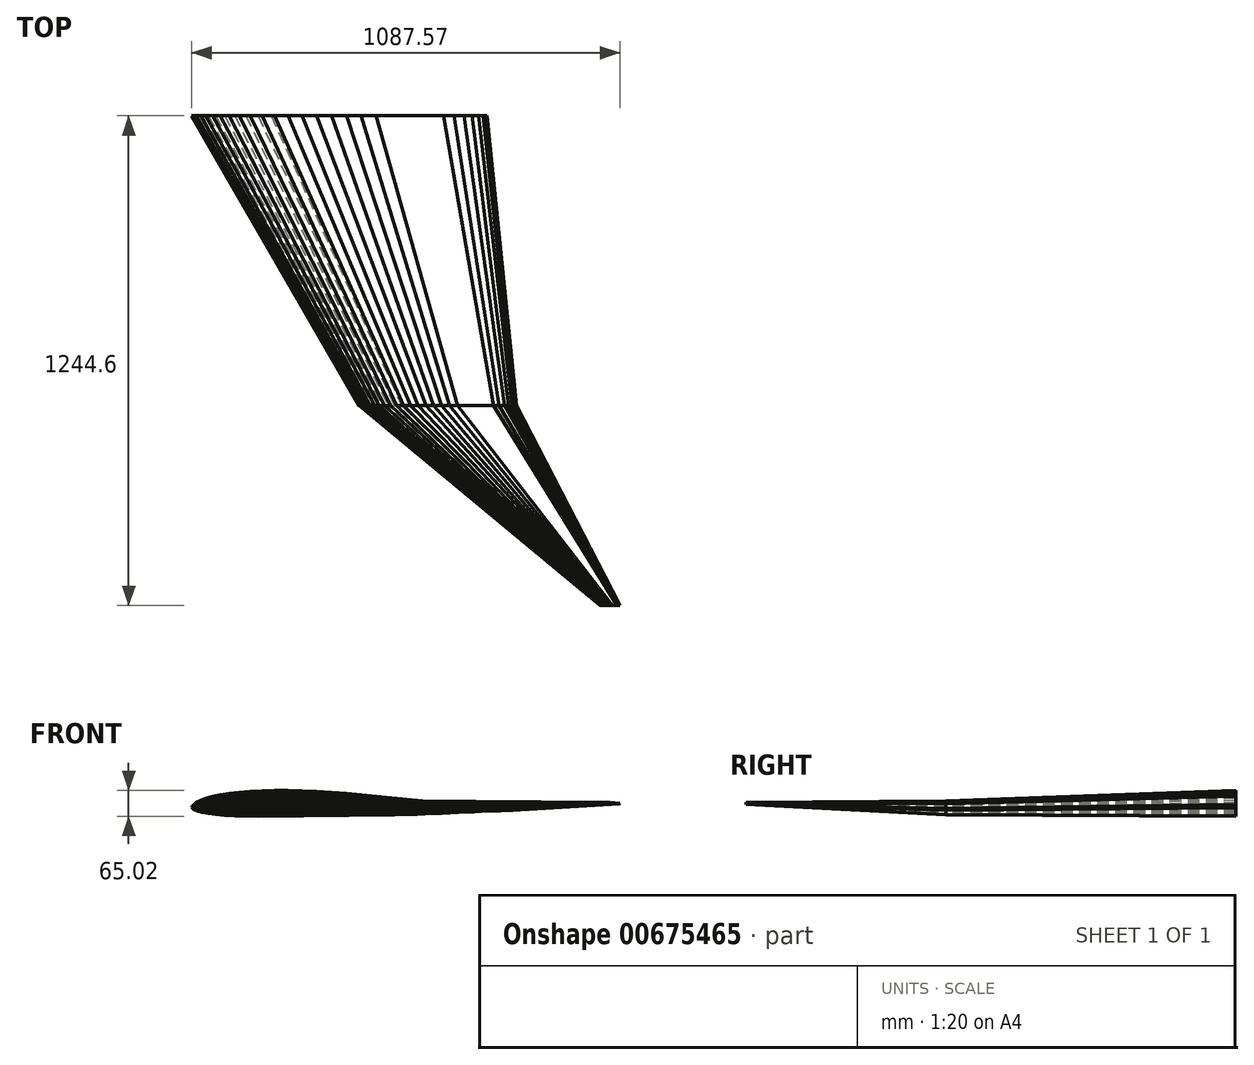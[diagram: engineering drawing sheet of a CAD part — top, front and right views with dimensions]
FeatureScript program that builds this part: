
annotation { "Feature Type Name" : "Feature", "Feature Type Description" : "" }
export const myFeature = defineFeature(function(context is Context, id is Id, definition is map)
    precondition{}
    {
        {
            var Q0;
            Q0=qCreatedBy(makeId("Front.planeOp"),FACE);
            var sketch = newSketch(context, id + "F0", { "sketchPlane" : qUnion([Q0])});
            skLineSegment(sketch, "E0", {"start": v(375, -10.05) * mm, "end": v(372.59, -10.06) * mm});
            skLineSegment(sketch, "E1", {"start": v(372.59, -10.06) * mm, "end": v(365.32, -10) * mm});
            skLineSegment(sketch, "E2", {"start": v(365.32, -10) * mm, "end": v(353.32, -9.6) * mm});
            skLineSegment(sketch, "E3", {"start": v(353.32, -9.6) * mm, "end": v(336.87, -8.71) * mm});
            skLineSegment(sketch, "E4", {"start": v(336.87, -8.71) * mm, "end": v(316.26, -7.24) * mm});
            skLineSegment(sketch, "E5", {"start": v(316.26, -7.24) * mm, "end": v(291.86, -5.09) * mm});
            skLineSegment(sketch, "E6", {"start": v(291.86, -5.09) * mm, "end": v(264.18, -2.25) * mm});
            skLineSegment(sketch, "E7", {"start": v(264.18, -2.25) * mm, "end": v(233.7, 1.18) * mm});
            skLineSegment(sketch, "E8", {"start": v(233.7, 1.18) * mm, "end": v(200.89, 5.09) * mm});
            skLineSegment(sketch, "E9", {"start": v(200.89, 5.09) * mm, "end": v(166.24, 9.3) * mm});
            skLineSegment(sketch, "E10", {"start": v(166.24, 9.3) * mm, "end": v(130.24, 13.62) * mm});
            skLineSegment(sketch, "E11", {"start": v(130.24, 13.62) * mm, "end": v(93.27, 17.8) * mm});
            skLineSegment(sketch, "E12", {"start": v(93.27, 17.8) * mm, "end": v(55.7, 21.63) * mm});
            skLineSegment(sketch, "E13", {"start": v(55.7, 21.63) * mm, "end": v(17.83, 25) * mm});
            skLineSegment(sketch, "E14", {"start": v(17.83, 25) * mm, "end": v(-20.02, 27.78) * mm});
            skLineSegment(sketch, "E15", {"start": v(-20.02, 27.78) * mm, "end": v(-57.5, 29.97) * mm});
            skLineSegment(sketch, "E16", {"start": v(-57.5, 29.97) * mm, "end": v(-94.23, 31.51) * mm});
            skLineSegment(sketch, "E17", {"start": v(-94.23, 31.51) * mm, "end": v(-129.86, 32.37) * mm});
            skLineSegment(sketch, "E18", {"start": v(-129.86, 32.37) * mm, "end": v(-164.03, 32.5) * mm});
            skLineSegment(sketch, "E19", {"start": v(-164.03, 32.5) * mm, "end": v(-196.4, 31.89) * mm});
            skLineSegment(sketch, "E20", {"start": v(-196.4, 31.89) * mm, "end": v(-226.7, 30.47) * mm});
            skLineSegment(sketch, "E21", {"start": v(-226.7, 30.47) * mm, "end": v(-254.68, 28.27) * mm});
            skLineSegment(sketch, "E22", {"start": v(-254.68, 28.27) * mm, "end": v(-280.12, 25.33) * mm});
            skLineSegment(sketch, "E23", {"start": v(-280.12, 25.33) * mm, "end": v(-302.8, 21.7) * mm});
            skLineSegment(sketch, "E24", {"start": v(-302.8, 21.7) * mm, "end": v(-322.57, 17.45) * mm});
            skLineSegment(sketch, "E25", {"start": v(-322.57, 17.45) * mm, "end": v(-339.3, 12.66) * mm});
            skLineSegment(sketch, "E26", {"start": v(-339.3, 12.66) * mm, "end": v(-352.9, 7.47) * mm});
            skLineSegment(sketch, "E27", {"start": v(-352.9, 7.47) * mm, "end": v(-363.34, 2.06) * mm});
            skLineSegment(sketch, "E28", {"start": v(-363.34, 2.06) * mm, "end": v(-370.58, -3.28) * mm});
            skLineSegment(sketch, "E29", {"start": v(-370.58, -3.28) * mm, "end": v(-374.56, -8.12) * mm});
            skLineSegment(sketch, "E30", {"start": v(-374.56, -8.12) * mm, "end": v(-375, -10.05) * mm});
            skLineSegment(sketch, "E31", {"start": v(-375, -10.05) * mm, "end": v(-374.42, -12) * mm});
            skLineSegment(sketch, "E32", {"start": v(-374.42, -12) * mm, "end": v(-369.82, -15.48) * mm});
            skLineSegment(sketch, "E33", {"start": v(-369.82, -15.48) * mm, "end": v(-361.28, -19.05) * mm});
            skLineSegment(sketch, "E34", {"start": v(-361.28, -19.05) * mm, "end": v(-349.03, -22.44) * mm});
            skLineSegment(sketch, "E35", {"start": v(-349.03, -22.44) * mm, "end": v(-333.25, -25.53) * mm});
            skLineSegment(sketch, "E36", {"start": v(-333.25, -25.53) * mm, "end": v(-314.1, -28.15) * mm});
            skLineSegment(sketch, "E37", {"start": v(-314.1, -28.15) * mm, "end": v(-291.71, -30.2) * mm});
            skLineSegment(sketch, "E38", {"start": v(-291.71, -30.2) * mm, "end": v(-266.22, -31.6) * mm});
            skLineSegment(sketch, "E39", {"start": v(-266.22, -31.6) * mm, "end": v(-237.8, -32.35) * mm});
            skLineSegment(sketch, "E40", {"start": v(-237.8, -32.35) * mm, "end": v(-206.66, -32.5) * mm});
            skLineSegment(sketch, "E41", {"start": v(-206.66, -32.5) * mm, "end": v(-173.08, -32.14) * mm});
            skLineSegment(sketch, "E42", {"start": v(-173.08, -32.14) * mm, "end": v(-137.42, -31.32) * mm});
            skLineSegment(sketch, "E43", {"start": v(-137.42, -31.32) * mm, "end": v(-100.01, -30.12) * mm});
            skLineSegment(sketch, "E44", {"start": v(-100.01, -30.12) * mm, "end": v(-61.28, -28.63) * mm});
            skLineSegment(sketch, "E45", {"start": v(-61.28, -28.63) * mm, "end": v(-21.66, -26.96) * mm});
            skLineSegment(sketch, "E46", {"start": v(-21.66, -26.96) * mm, "end": v(18.39, -25.17) * mm});
            skLineSegment(sketch, "E47", {"start": v(18.39, -25.17) * mm, "end": v(58.39, -23.36) * mm});
            skLineSegment(sketch, "E48", {"start": v(58.39, -23.36) * mm, "end": v(97.83, -21.59) * mm});
            skLineSegment(sketch, "E49", {"start": v(97.83, -21.59) * mm, "end": v(136.25, -19.88) * mm});
            skLineSegment(sketch, "E50", {"start": v(136.25, -19.88) * mm, "end": v(173.15, -18.28) * mm});
            skLineSegment(sketch, "E51", {"start": v(173.15, -18.28) * mm, "end": v(208.1, -16.81) * mm});
            skLineSegment(sketch, "E52", {"start": v(208.1, -16.81) * mm, "end": v(240.67, -15.48) * mm});
            skLineSegment(sketch, "E53", {"start": v(240.67, -15.48) * mm, "end": v(270.44, -14.32) * mm});
            skLineSegment(sketch, "E54", {"start": v(270.44, -14.32) * mm, "end": v(297.05, -13.32) * mm});
            skLineSegment(sketch, "E55", {"start": v(297.05, -13.32) * mm, "end": v(320.16, -12.48) * mm});
            skLineSegment(sketch, "E56", {"start": v(320.16, -12.48) * mm, "end": v(339.47, -11.77) * mm});
            skLineSegment(sketch, "E57", {"start": v(339.47, -11.77) * mm, "end": v(354.75, -11.17) * mm});
            skLineSegment(sketch, "E58", {"start": v(354.75, -11.17) * mm, "end": v(365.83, -10.62) * mm});
            skLineSegment(sketch, "E59", {"start": v(365.83, -10.62) * mm, "end": v(372.65, -10.2) * mm});
            skLineSegment(sketch, "E60", {"start": v(372.65, -10.2) * mm, "end": v(375, -10.05) * mm});
            skLineSegment(sketch, "E61", {"start": v(-375, -10.05) * mm, "end": v(375, -10.05) * mm});
            skSolve(sketch);
        }
        {
            var Q0;
            Q0=qCreatedBy(makeId("Front.planeOp"),FACE);
            cPlane(context, id + "F1", {"entities" : qUnion([Q0]), "cplaneType" : CPlaneType.OFFSET, "offset" : 736.6 * mm, "width" : 152.4 * mm, "height" : 152.4 * mm});
        }
        {
            var Q0;
            Q0=qCreatedBy(id+"F1.planeOp",FACE);
            var sketch = newSketch(context, id + "F2", { "sketchPlane" : qUnion([Q0])});
            skLineSegment(sketch, "E62", {"start": v(450.55, -16.79) * mm, "end": v(449.26, -16.8) * mm});
            skLineSegment(sketch, "E63", {"start": v(449.26, -16.8) * mm, "end": v(445.39, -16.76) * mm});
            skLineSegment(sketch, "E64", {"start": v(445.39, -16.76) * mm, "end": v(438.99, -16.55) * mm});
            skLineSegment(sketch, "E65", {"start": v(438.99, -16.55) * mm, "end": v(430.21, -16.08) * mm});
            skLineSegment(sketch, "E66", {"start": v(430.21, -16.08) * mm, "end": v(419.22, -15.3) * mm});
            skLineSegment(sketch, "E67", {"start": v(419.22, -15.3) * mm, "end": v(406.2, -14.14) * mm});
            skLineSegment(sketch, "E68", {"start": v(406.2, -14.14) * mm, "end": v(391.45, -12.63) * mm});
            skLineSegment(sketch, "E69", {"start": v(391.45, -12.63) * mm, "end": v(375.19, -10.8) * mm});
            skLineSegment(sketch, "E70", {"start": v(375.19, -10.8) * mm, "end": v(357.69, -8.72) * mm});
            skLineSegment(sketch, "E71", {"start": v(357.69, -8.72) * mm, "end": v(339.21, -6.47) * mm});
            skLineSegment(sketch, "E72", {"start": v(339.21, -6.47) * mm, "end": v(320, -4.17) * mm});
            skLineSegment(sketch, "E73", {"start": v(320, -4.17) * mm, "end": v(300.3, -1.94) * mm});
            skLineSegment(sketch, "E74", {"start": v(300.3, -1.94) * mm, "end": v(280.25, 0.1) * mm});
            skLineSegment(sketch, "E75", {"start": v(280.25, 0.1) * mm, "end": v(260.06, 1.9) * mm});
            skLineSegment(sketch, "E76", {"start": v(260.06, 1.9) * mm, "end": v(239.87, 3.39) * mm});
            skLineSegment(sketch, "E77", {"start": v(239.87, 3.39) * mm, "end": v(219.89, 4.55) * mm});
            skLineSegment(sketch, "E78", {"start": v(219.89, 4.55) * mm, "end": v(200.3, 5.38) * mm});
            skLineSegment(sketch, "E79", {"start": v(200.3, 5.38) * mm, "end": v(181.29, 5.83) * mm});
            skLineSegment(sketch, "E80", {"start": v(181.29, 5.83) * mm, "end": v(163.07, 5.9) * mm});
            skLineSegment(sketch, "E81", {"start": v(163.07, 5.9) * mm, "end": v(145.8, 5.58) * mm});
            skLineSegment(sketch, "E82", {"start": v(145.8, 5.58) * mm, "end": v(129.64, 4.82) * mm});
            skLineSegment(sketch, "E83", {"start": v(129.64, 4.82) * mm, "end": v(114.72, 3.65) * mm});
            skLineSegment(sketch, "E84", {"start": v(114.72, 3.65) * mm, "end": v(101.15, 2.08) * mm});
            skLineSegment(sketch, "E85", {"start": v(101.15, 2.08) * mm, "end": v(89.05, 0.14) * mm});
            skLineSegment(sketch, "E86", {"start": v(89.05, 0.14) * mm, "end": v(78.5, -2.12) * mm});
            skLineSegment(sketch, "E87", {"start": v(78.5, -2.12) * mm, "end": v(69.6, -4.68) * mm});
            skLineSegment(sketch, "E88", {"start": v(69.6, -4.68) * mm, "end": v(62.34, -7.45) * mm});
            skLineSegment(sketch, "E89", {"start": v(62.34, -7.45) * mm, "end": v(56.77, -10.33) * mm});
            skLineSegment(sketch, "E90", {"start": v(56.77, -10.33) * mm, "end": v(52.9, -13.18) * mm});
            skLineSegment(sketch, "E91", {"start": v(52.9, -13.18) * mm, "end": v(50.79, -15.76) * mm});
            skLineSegment(sketch, "E92", {"start": v(50.79, -15.76) * mm, "end": v(50.55, -16.79) * mm});
            skLineSegment(sketch, "E93", {"start": v(50.55, -16.79) * mm, "end": v(50.86, -17.83) * mm});
            skLineSegment(sketch, "E94", {"start": v(50.86, -17.83) * mm, "end": v(53.3, -19.68) * mm});
            skLineSegment(sketch, "E95", {"start": v(53.3, -19.68) * mm, "end": v(57.87, -21.59) * mm});
            skLineSegment(sketch, "E96", {"start": v(57.87, -21.59) * mm, "end": v(64.4, -23.4) * mm});
            skLineSegment(sketch, "E97", {"start": v(64.4, -23.4) * mm, "end": v(72.81, -25.04) * mm});
            skLineSegment(sketch, "E98", {"start": v(72.81, -25.04) * mm, "end": v(83.03, -26.44) * mm});
            skLineSegment(sketch, "E99", {"start": v(83.03, -26.44) * mm, "end": v(94.97, -27.53) * mm});
            skLineSegment(sketch, "E100", {"start": v(94.97, -27.53) * mm, "end": v(108.57, -28.28) * mm});
            skLineSegment(sketch, "E101", {"start": v(108.57, -28.28) * mm, "end": v(123.72, -28.68) * mm});
            skLineSegment(sketch, "E102", {"start": v(123.72, -28.68) * mm, "end": v(140.33, -28.77) * mm});
            skLineSegment(sketch, "E103", {"start": v(140.33, -28.77) * mm, "end": v(158.24, -28.57) * mm});
            skLineSegment(sketch, "E104", {"start": v(158.24, -28.57) * mm, "end": v(177.26, -28.13) * mm});
            skLineSegment(sketch, "E105", {"start": v(177.26, -28.13) * mm, "end": v(197.2, -27.5) * mm});
            skLineSegment(sketch, "E106", {"start": v(197.2, -27.5) * mm, "end": v(217.87, -26.7) * mm});
            skLineSegment(sketch, "E107", {"start": v(217.87, -26.7) * mm, "end": v(239, -25.8) * mm});
            skLineSegment(sketch, "E108", {"start": v(239, -25.8) * mm, "end": v(260.36, -24.86) * mm});
            skLineSegment(sketch, "E109", {"start": v(260.36, -24.86) * mm, "end": v(281.69, -23.89) * mm});
            skLineSegment(sketch, "E110", {"start": v(281.69, -23.89) * mm, "end": v(302.73, -22.94) * mm});
            skLineSegment(sketch, "E111", {"start": v(302.73, -22.94) * mm, "end": v(323.21, -22.03) * mm});
            skLineSegment(sketch, "E112", {"start": v(323.21, -22.03) * mm, "end": v(342.9, -21.18) * mm});
            skLineSegment(sketch, "E113", {"start": v(342.9, -21.18) * mm, "end": v(361.54, -20.4) * mm});
            skLineSegment(sketch, "E114", {"start": v(361.54, -20.4) * mm, "end": v(378.9, -19.69) * mm});
            skLineSegment(sketch, "E115", {"start": v(378.9, -19.69) * mm, "end": v(394.79, -19.07) * mm});
            skLineSegment(sketch, "E116", {"start": v(394.79, -19.07) * mm, "end": v(408.98, -18.54) * mm});
            skLineSegment(sketch, "E117", {"start": v(408.98, -18.54) * mm, "end": v(421.3, -18.09) * mm});
            skLineSegment(sketch, "E118", {"start": v(421.3, -18.09) * mm, "end": v(431.6, -17.7) * mm});
            skLineSegment(sketch, "E119", {"start": v(431.6, -17.7) * mm, "end": v(439.75, -17.39) * mm});
            skLineSegment(sketch, "E120", {"start": v(439.75, -17.39) * mm, "end": v(445.66, -17.1) * mm});
            skLineSegment(sketch, "E121", {"start": v(445.66, -17.1) * mm, "end": v(449.3, -16.87) * mm});
            skLineSegment(sketch, "E122", {"start": v(449.3, -16.87) * mm, "end": v(450.55, -16.79) * mm});
            skLineSegment(sketch, "E123", {"start": v(50.55, -16.79) * mm, "end": v(450.55, -16.79) * mm});
            skSolve(sketch);
        }
        {
            var Q0;
            Q0=qCreatedBy(id+"F1.planeOp",FACE);
            cPlane(context, id + "F3", {"entities" : qUnion([Q0]), "cplaneType" : CPlaneType.OFFSET, "offset" : 508 * mm, "width" : 152.4 * mm, "height" : 152.4 * mm});
        }
        {
            var Q0;
            Q0=qCreatedBy(id+"F3.planeOp",FACE);
            var sketch = newSketch(context, id + "F4", { "sketchPlane" : qUnion([Q0])});
            skLineSegment(sketch, "E124", {"start": v(712.57, -0.67) * mm, "end": v(712.41, -0.67) * mm});
            skLineSegment(sketch, "E125", {"start": v(712.41, -0.67) * mm, "end": v(711.93, -0.67) * mm});
            skLineSegment(sketch, "E126", {"start": v(711.93, -0.67) * mm, "end": v(711.13, -0.64) * mm});
            skLineSegment(sketch, "E127", {"start": v(711.13, -0.64) * mm, "end": v(710.03, -0.58) * mm});
            skLineSegment(sketch, "E128", {"start": v(710.03, -0.58) * mm, "end": v(708.66, -0.48) * mm});
            skLineSegment(sketch, "E129", {"start": v(708.66, -0.48) * mm, "end": v(707.03, -0.34) * mm});
            skLineSegment(sketch, "E130", {"start": v(707.03, -0.34) * mm, "end": v(705.19, -0.15) * mm});
            skLineSegment(sketch, "E131", {"start": v(705.19, -0.15) * mm, "end": v(703.15, 0.08) * mm});
            skLineSegment(sketch, "E132", {"start": v(703.15, 0.08) * mm, "end": v(700.97, 0.34) * mm});
            skLineSegment(sketch, "E133", {"start": v(700.97, 0.34) * mm, "end": v(698.66, 0.62) * mm});
            skLineSegment(sketch, "E134", {"start": v(698.66, 0.62) * mm, "end": v(696.26, 0.9) * mm});
            skLineSegment(sketch, "E135", {"start": v(696.26, 0.9) * mm, "end": v(693.8, 1.19) * mm});
            skLineSegment(sketch, "E136", {"start": v(693.8, 1.19) * mm, "end": v(691.29, 1.44) * mm});
            skLineSegment(sketch, "E137", {"start": v(691.29, 1.44) * mm, "end": v(688.76, 1.67) * mm});
            skLineSegment(sketch, "E138", {"start": v(688.76, 1.67) * mm, "end": v(686.24, 1.85) * mm});
            skLineSegment(sketch, "E139", {"start": v(686.24, 1.85) * mm, "end": v(683.74, 2) * mm});
            skLineSegment(sketch, "E140", {"start": v(683.74, 2) * mm, "end": v(681.3, 2.1) * mm});
            skLineSegment(sketch, "E141", {"start": v(681.3, 2.1) * mm, "end": v(678.92, 2.16) * mm});
            skLineSegment(sketch, "E142", {"start": v(678.92, 2.16) * mm, "end": v(676.64, 2.17) * mm});
            skLineSegment(sketch, "E143", {"start": v(676.64, 2.17) * mm, "end": v(674.48, 2.13) * mm});
            skLineSegment(sketch, "E144", {"start": v(674.48, 2.13) * mm, "end": v(672.46, 2.03) * mm});
            skLineSegment(sketch, "E145", {"start": v(672.46, 2.03) * mm, "end": v(670.6, 1.88) * mm});
            skLineSegment(sketch, "E146", {"start": v(670.6, 1.88) * mm, "end": v(668.9, 1.69) * mm});
            skLineSegment(sketch, "E147", {"start": v(668.9, 1.69) * mm, "end": v(667.39, 1.45) * mm});
            skLineSegment(sketch, "E148", {"start": v(667.39, 1.45) * mm, "end": v(666.07, 1.16) * mm});
            skLineSegment(sketch, "E149", {"start": v(666.07, 1.16) * mm, "end": v(664.95, 0.84) * mm});
            skLineSegment(sketch, "E150", {"start": v(664.95, 0.84) * mm, "end": v(664.05, 0.5) * mm});
            skLineSegment(sketch, "E151", {"start": v(664.05, 0.5) * mm, "end": v(663.35, 0.14) * mm});
            skLineSegment(sketch, "E152", {"start": v(663.35, 0.14) * mm, "end": v(662.87, -0.22) * mm});
            skLineSegment(sketch, "E153", {"start": v(662.87, -0.22) * mm, "end": v(662.6, -0.54) * mm});
            skLineSegment(sketch, "E154", {"start": v(662.6, -0.54) * mm, "end": v(662.57, -0.67) * mm});
            skLineSegment(sketch, "E155", {"start": v(662.57, -0.67) * mm, "end": v(662.61, -0.8) * mm});
            skLineSegment(sketch, "E156", {"start": v(662.61, -0.8) * mm, "end": v(662.92, -1.03) * mm});
            skLineSegment(sketch, "E157", {"start": v(662.92, -1.03) * mm, "end": v(663.49, -1.27) * mm});
            skLineSegment(sketch, "E158", {"start": v(663.49, -1.27) * mm, "end": v(664.3, -1.5) * mm});
            skLineSegment(sketch, "E159", {"start": v(664.3, -1.5) * mm, "end": v(665.36, -1.7) * mm});
            skLineSegment(sketch, "E160", {"start": v(665.36, -1.7) * mm, "end": v(666.63, -1.88) * mm});
            skLineSegment(sketch, "E161", {"start": v(666.63, -1.88) * mm, "end": v(668.13, -2.01) * mm});
            skLineSegment(sketch, "E162", {"start": v(668.13, -2.01) * mm, "end": v(669.83, -2.1) * mm});
            skLineSegment(sketch, "E163", {"start": v(669.83, -2.1) * mm, "end": v(671.72, -2.16) * mm});
            skLineSegment(sketch, "E164", {"start": v(671.72, -2.16) * mm, "end": v(673.8, -2.17) * mm});
            skLineSegment(sketch, "E165", {"start": v(673.8, -2.17) * mm, "end": v(676.04, -2.14) * mm});
            skLineSegment(sketch, "E166", {"start": v(676.04, -2.14) * mm, "end": v(678.41, -2.09) * mm});
            skLineSegment(sketch, "E167", {"start": v(678.41, -2.09) * mm, "end": v(680.9, -2) * mm});
            skLineSegment(sketch, "E168", {"start": v(680.9, -2) * mm, "end": v(683.49, -1.9) * mm});
            skLineSegment(sketch, "E169", {"start": v(683.49, -1.9) * mm, "end": v(686.13, -1.8) * mm});
            skLineSegment(sketch, "E170", {"start": v(686.13, -1.8) * mm, "end": v(688.8, -1.68) * mm});
            skLineSegment(sketch, "E171", {"start": v(688.8, -1.68) * mm, "end": v(691.47, -1.56) * mm});
            skLineSegment(sketch, "E172", {"start": v(691.47, -1.56) * mm, "end": v(694.1, -1.44) * mm});
            skLineSegment(sketch, "E173", {"start": v(694.1, -1.44) * mm, "end": v(696.66, -1.33) * mm});
            skLineSegment(sketch, "E174", {"start": v(696.66, -1.33) * mm, "end": v(699.12, -1.22) * mm});
            skLineSegment(sketch, "E175", {"start": v(699.12, -1.22) * mm, "end": v(701.45, -1.12) * mm});
            skLineSegment(sketch, "E176", {"start": v(701.45, -1.12) * mm, "end": v(703.62, -1.03) * mm});
            skLineSegment(sketch, "E177", {"start": v(703.62, -1.03) * mm, "end": v(705.6, -0.95) * mm});
            skLineSegment(sketch, "E178", {"start": v(705.6, -0.95) * mm, "end": v(707.38, -0.89) * mm});
            skLineSegment(sketch, "E179", {"start": v(707.38, -0.89) * mm, "end": v(708.92, -0.83) * mm});
            skLineSegment(sketch, "E180", {"start": v(708.92, -0.83) * mm, "end": v(710.2, -0.78) * mm});
            skLineSegment(sketch, "E181", {"start": v(710.2, -0.78) * mm, "end": v(711.22, -0.74) * mm});
            skLineSegment(sketch, "E182", {"start": v(711.22, -0.74) * mm, "end": v(711.96, -0.7) * mm});
            skLineSegment(sketch, "E183", {"start": v(711.96, -0.7) * mm, "end": v(712.42, -0.68) * mm});
            skLineSegment(sketch, "E184", {"start": v(712.42, -0.68) * mm, "end": v(712.57, -0.67) * mm});
            skLineSegment(sketch, "E185", {"start": v(662.57, -0.67) * mm, "end": v(712.57, -0.67) * mm});
            skSolve(sketch);
        }
        {
            var Q0;
            {var subQ4=sQuery(id+"F0.wireOp",EDGE,"E2");Q0=makeQuery(id+"F0.imprint","IMPRINT",FACE,{"disambiguationData":[TD([[makeQuery(id+"F0.imprint","IMPRINT",EDGE,{"derivedFrom":subQ4}),1.0]])]});}
            var Q1;
            {var subQ4=sQuery(id+"F2.wireOp",EDGE,"E64");Q1=makeQuery(id+"F2.imprint","IMPRINT",FACE,{"disambiguationData":[TD([[makeQuery(id+"F2.imprint","IMPRINT",EDGE,{"derivedFrom":subQ4}),1.0]])]});}
            loft(context, id + "F5", {"sheetProfilesArray" : [{ "sheetProfileEntities" : qUnion([Q0]) }, { "sheetProfileEntities" : qUnion([Q1]) }]});
        }
        {
            var Q1;
            {var subQ1=sQuery(id+"F0.wireOp",EDGE,"E0");Q1=makeQuery(id+"F0.imprint","IMPRINT",FACE,{"disambiguationData":[TD([[makeQuery(id+"F0.imprint","IMPRINT",EDGE,{"derivedFrom":subQ1}),1.0]])]});}
            var Q2;
            {var subQ1=sQuery(id+"F2.wireOp",EDGE,"E62");Q2=makeQuery(id+"F2.imprint","IMPRINT",FACE,{"disambiguationData":[TD([[makeQuery(id+"F2.imprint","IMPRINT",EDGE,{"derivedFrom":subQ1}),1.0]])]});}
            loft(context, id + "F6", {"operationType" : NewBodyOperationType.ADD, "sheetProfilesArray" : [{ "sheetProfileEntities" : qUnion([Q1]) }, { "sheetProfileEntities" : qUnion([Q2]) }]});
        }
        {
            var Q1;
            {var subQ4=sQuery(id+"F2.wireOp",EDGE,"E64");Q1=makeQuery(id+"F2.imprint","IMPRINT",FACE,{"disambiguationData":[TD([[makeQuery(id+"F2.imprint","IMPRINT",EDGE,{"derivedFrom":subQ4}),1.0]])]});}
            var Q2;
            {var subQ4=sQuery(id+"F4.wireOp",EDGE,"E126");Q2=makeQuery(id+"F4.imprint","IMPRINT",FACE,{"disambiguationData":[TD([[makeQuery(id+"F4.imprint","IMPRINT",EDGE,{"derivedFrom":subQ4}),1.0]])]});}
            loft(context, id + "F7", {"operationType" : NewBodyOperationType.ADD, "sheetProfilesArray" : [{ "sheetProfileEntities" : qUnion([Q1]) }, { "sheetProfileEntities" : qUnion([Q2]) }]});
        }
        {
            var Q1;
            {var subQ1=sQuery(id+"F4.wireOp",EDGE,"E124");Q1=makeQuery(id+"F4.imprint","IMPRINT",FACE,{"disambiguationData":[TD([[makeQuery(id+"F4.imprint","IMPRINT",EDGE,{"derivedFrom":subQ1}),1.0]])]});}
            var Q2;
            {var subQ1=sQuery(id+"F2.wireOp",EDGE,"E62");Q2=makeQuery(id+"F2.imprint","IMPRINT",FACE,{"disambiguationData":[TD([[makeQuery(id+"F2.imprint","IMPRINT",EDGE,{"derivedFrom":subQ1}),1.0]])]});}
            loft(context, id + "F8", {"operationType" : NewBodyOperationType.ADD, "sheetProfilesArray" : [{ "sheetProfileEntities" : qUnion([Q1]) }, { "sheetProfileEntities" : qUnion([Q2]) }]});
        }
    });
